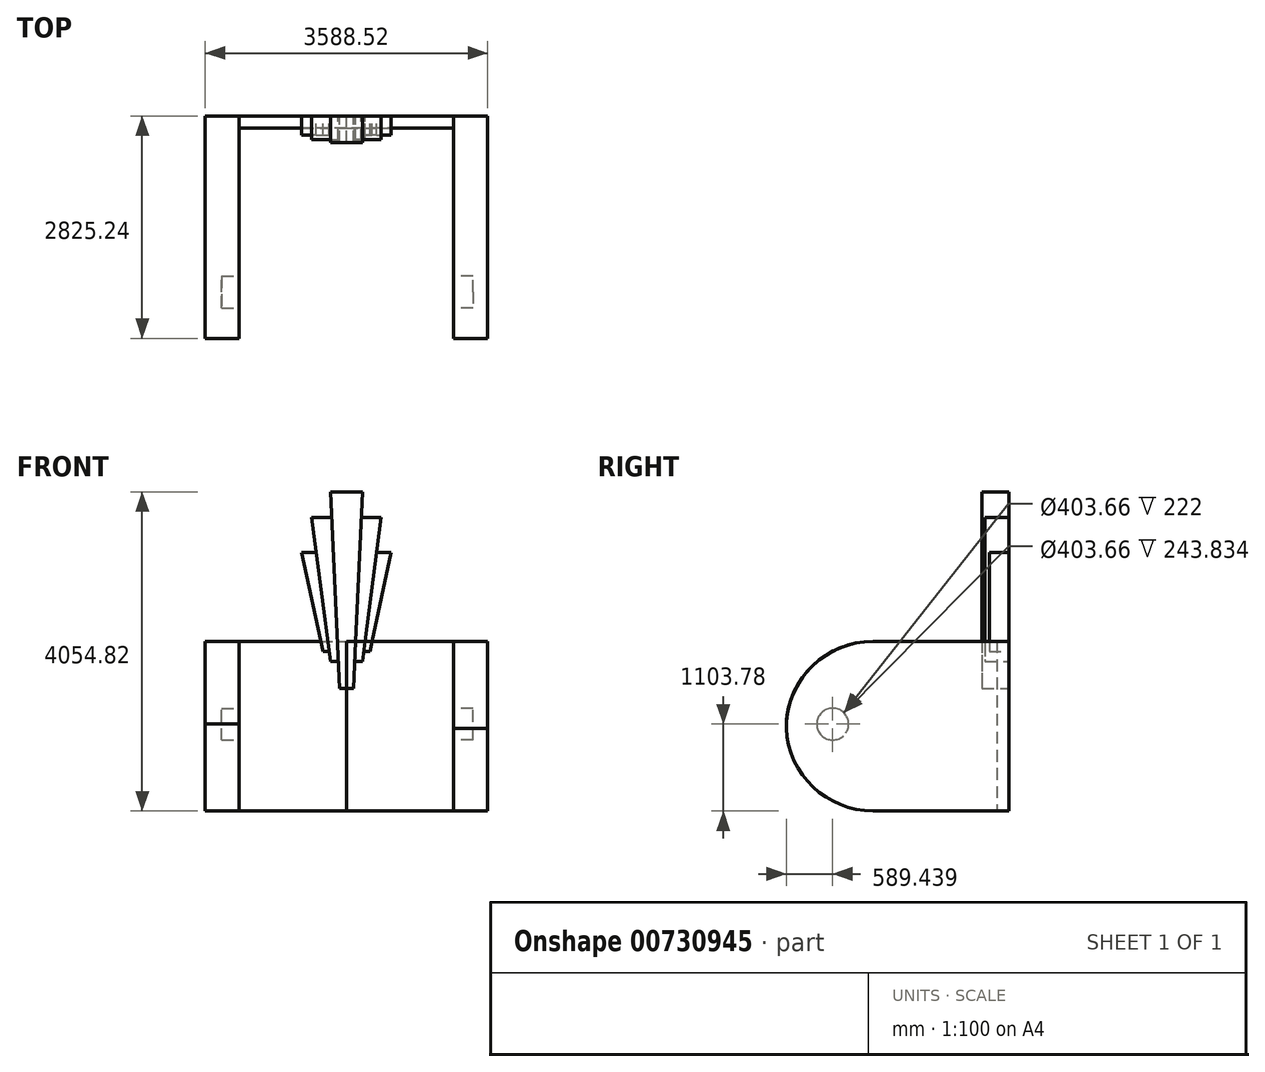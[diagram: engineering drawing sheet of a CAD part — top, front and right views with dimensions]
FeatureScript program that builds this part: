
annotation { "Feature Type Name" : "Feature", "Feature Type Description" : "" }
export const myFeature = defineFeature(function(context is Context, id is Id, definition is map)
    precondition{}
    {
        {
            var Q0;
            Q0=qCreatedBy(makeId("Front.planeOp"),FACE);
            var sketch = newSketch(context, id + "F0", { "sketchPlane" : qUnion([Q0])});
            skLineSegment(sketch, "E0", {"start": v(-1794.26, 1172.74) * mm, "end": v(1362.58, 1172.74) * mm});
            skLineSegment(sketch, "E1", {"start": v(1362.58, -982.7) * mm, "end": v(1362.58, 1172.74) * mm});
            skLineSegment(sketch, "E2", {"start": v(1362.58, -982.7) * mm, "end": v(-1794.26, -982.7) * mm});
            skLineSegment(sketch, "E3", {"start": v(-1794.26, 1172.74) * mm, "end": v(-1794.26, -982.7) * mm});
            skLineSegment(sketch, "E4", {"start": v(0, 1172.74) * mm, "end": v(0, -982.7) * mm});
            skLineSegment(sketch, "E5.MirrorCS", {"start": v(1794.26, 1172.74) * mm, "end": v(1794.26, -982.7) * mm});
            skLineSegment(sketch, "E6.MirrorCS", {"start": v(-1362.58, -982.7) * mm, "end": v(-1362.58, 1172.74) * mm});
            skLineSegment(sketch, "E7", {"start": v(1362.58, 1172.74) * mm, "end": v(1794.26, 1172.74) * mm});
            skLineSegment(sketch, "E8", {"start": v(1362.58, -982.7) * mm, "end": v(1794.26, -982.7) * mm});
            skSolve(sketch);
        }
        {
            var Q0;
            {var subQ0=sQuery(id+"F0.wireOp",EDGE,"E3");Q0=makeQuery(id+"F0.imprint","IMPRINT",FACE,{"disambiguationData":[TD([[makeQuery(id+"F0.imprint","IMPRINT",EDGE,{"derivedFrom":subQ0}),1.0]])]});}
            extrude(context, id + "F1", {"entities" : qUnion([Q0]), "depth" : 2825.24 * mm, "offsetDistance" : 25.4 * mm});
        }
        {
            var Q0;
            {var subQ0=sQuery(id+"F0.wireOp",EDGE,"E1");Q0=makeQuery(id+"F0.imprint","IMPRINT",FACE,{"disambiguationData":[TD([[makeQuery(id+"F0.imprint","IMPRINT",EDGE,{"derivedFrom":subQ0}),1.0]])]});}
            extrude(context, id + "F2", {"entities" : qUnion([Q0]), "depth" : 152.4 * mm, "offsetDistance" : 25.4 * mm});
        }
        {
            var Q0;
            Q0=makeQuery(id+"F1.opExtrude","CAP_EDGE",EDGE,{"disambiguationData":[OSD([sQuery(id+"F0.wireOp",EDGE,"E2")])],"isStart":false});
            fillet(context, id + "F3", {"entities" : qUnion([Q0]), "radius" : 1103.78 * mm, "tangentPropagation" : true, "allowEdgeOverflow" : false});
        }
        {
            var Q0;
            Q0=makeQuery(id+"F1.opExtrude","CAP_EDGE",EDGE,{"disambiguationData":[OSD([sQuery(id+"F0.wireOp",EDGE,"E0")])],"isStart":false});
            fillet(context, id + "F4", {"entities" : qUnion([Q0]), "radius" : 1103.78 * mm, "tangentPropagation" : true, "allowEdgeOverflow" : false});
        }
        {
            var Q0;
            Q0=makeQuery(id+"F2.opExtrude","CAP_FACE",FACE,{"disambiguationData":[OSD([sQuery(id+"F0.wireOp",EDGE,"E0"),sQuery(id+"F0.wireOp",EDGE,"E1"),sQuery(id+"F0.wireOp",EDGE,"E2"),sQuery(id+"F0.wireOp",EDGE,"sX38Ko4N-RZgO-N5hY-b6du-1SKDG1pY7xjY")])],"isStart":true});
            var sketch = newSketch(context, id + "F5", { "sketchPlane" : qUnion([Q0])});
            skLineSegment(sketch, "E9", {"start": v(0, 3072.12) * mm, "end": v(-202.15, 3072.12) * mm});
            skLineSegment(sketch, "E10", {"start": v(-202.15, 3072.12) * mm, "end": v(-89.06, 571.59) * mm});
            skLineSegment(sketch, "E11", {"start": v(-89.06, 571.59) * mm, "end": v(0, 571.59) * mm});
            skLineSegment(sketch, "E12.MirrorCS", {"start": v(202.15, 3072.12) * mm, "end": v(89.06, 571.59) * mm});
            skLineSegment(sketch, "E13.MirrorCS", {"start": v(0, 3072.12) * mm, "end": v(202.15, 3072.12) * mm});
            skLineSegment(sketch, "E14.MirrorCS", {"start": v(89.06, 571.59) * mm, "end": v(0, 571.59) * mm});
            skLineSegment(sketch, "E15", {"start": v(-187.3, 2743.87) * mm, "end": v(-442.01, 2743.87) * mm});
            skLineSegment(sketch, "E16", {"start": v(-442.01, 2743.87) * mm, "end": v(-202.15, 918.12) * mm});
            skLineSegment(sketch, "E17", {"start": v(-202.15, 918.12) * mm, "end": v(-104.73, 918.12) * mm});
            skLineSegment(sketch, "E18", {"start": v(-384.26, 2304.3) * mm, "end": v(-568.58, 2304.3) * mm});
            skLineSegment(sketch, "E19", {"start": v(-568.58, 2304.3) * mm, "end": v(-296.4, 1047.23) * mm});
            skLineSegment(sketch, "E20", {"start": v(-296.4, 1047.23) * mm, "end": v(-219.11, 1047.23) * mm});
            skLineSegment(sketch, "E21.MirrorCS", {"start": v(187.3, 2743.87) * mm, "end": v(442.01, 2743.87) * mm});
            skLineSegment(sketch, "E22.MirrorCS", {"start": v(442.01, 2743.87) * mm, "end": v(202.15, 918.12) * mm});
            skLineSegment(sketch, "E23.MirrorCS", {"start": v(384.26, 2304.3) * mm, "end": v(568.58, 2304.3) * mm});
            skLineSegment(sketch, "E24.MirrorCS", {"start": v(568.58, 2304.3) * mm, "end": v(296.4, 1047.23) * mm});
            skLineSegment(sketch, "E25.MirrorCS", {"start": v(296.4, 1047.23) * mm, "end": v(219.11, 1047.23) * mm});
            skLineSegment(sketch, "E26.MirrorCS", {"start": v(202.15, 918.12) * mm, "end": v(104.73, 918.12) * mm});
            skSolve(sketch);
        }
        {
            var Q0;
            {var subQ8=sQuery(id+"F5.wireOp",EDGE,"E9");Q0=makeQuery(id+"F5.imprint","IMPRINT",FACE,{"disambiguationData":[TD([[makeQuery(id+"F5.imprint","IMPRINT",EDGE,{"derivedFrom":subQ8}),1.0]])]});}
            extrude(context, id + "F6", {"entities" : qUnion([Q0]), "oppositeDirection" : true, "depth" : 337.82 * mm, "offsetDistance" : 25.4 * mm});
        }
        {
            var Q0;
            {var subQ0=sQuery(id+"F5.wireOp",EDGE,"E11");Q0=makeQuery(id+"F5.imprint","IMPRINT",FACE,{"disambiguationData":[TD([[makeQuery(id+"F5.imprint","IMPRINT",EDGE,{"derivedFrom":subQ0}),1.0]])]});}
            extrude(context, id + "F7", {"entities" : qUnion([Q0]), "oppositeDirection" : true, "depth" : 337.82 * mm, "offsetDistance" : 25.4 * mm});
        }
        {
            var Q0;
            {var subQ4=sQuery(id+"F5.wireOp",EDGE,"E15");Q0=makeQuery(id+"F5.imprint","IMPRINT",FACE,{"disambiguationData":[TD([[makeQuery(id+"F5.imprint","IMPRINT",EDGE,{"derivedFrom":subQ4}),1.0]])]});}
            extrude(context, id + "F8", {"entities" : qUnion([Q0]), "oppositeDirection" : true, "depth" : 299.72 * mm, "offsetDistance" : 25.4 * mm});
        }
        {
            var Q0;
            {var subQ0=sQuery(id+"F5.wireOp",EDGE,"E17");Q0=makeQuery(id+"F5.imprint","IMPRINT",FACE,{"disambiguationData":[TD([[makeQuery(id+"F5.imprint","IMPRINT",EDGE,{"derivedFrom":subQ0}),1.0]])]});}
            extrude(context, id + "F9", {"entities" : qUnion([Q0]), "oppositeDirection" : true, "depth" : 299.72 * mm, "offsetDistance" : 25.4 * mm});
        }
        {
            var Q0;
            {var subQ4=sQuery(id+"F5.wireOp",EDGE,"E21.MirrorCS");Q0=makeQuery(id+"F5.imprint","IMPRINT",FACE,{"disambiguationData":[TD([[makeQuery(id+"F5.imprint","IMPRINT",EDGE,{"derivedFrom":subQ4}),-1.0]])]});}
            extrude(context, id + "F10", {"entities" : qUnion([Q0]), "oppositeDirection" : true, "depth" : 299.72 * mm, "offsetDistance" : 25.4 * mm});
        }
        {
            var Q0;
            {var subQ0=sQuery(id+"F5.wireOp",EDGE,"E26.MirrorCS");Q0=makeQuery(id+"F5.imprint","IMPRINT",FACE,{"disambiguationData":[TD([[makeQuery(id+"F5.imprint","IMPRINT",EDGE,{"derivedFrom":subQ0}),-1.0]])]});}
            extrude(context, id + "F11", {"entities" : qUnion([Q0]), "oppositeDirection" : true, "depth" : 299.72 * mm, "offsetDistance" : 25.4 * mm});
        }
        {
            var Q0;
            {var subQ0=sQuery(id+"F5.wireOp",EDGE,"E18");Q0=makeQuery(id+"F5.imprint","IMPRINT",FACE,{"disambiguationData":[TD([[makeQuery(id+"F5.imprint","IMPRINT",EDGE,{"derivedFrom":subQ0}),1.0]])]});}
            extrude(context, id + "F12", {"entities" : qUnion([Q0]), "oppositeDirection" : true, "depth" : 246.38 * mm, "offsetDistance" : 25.4 * mm});
        }
        {
            var Q0;
            {var subQ0=sQuery(id+"F5.wireOp",EDGE,"E20");Q0=makeQuery(id+"F5.imprint","IMPRINT",FACE,{"disambiguationData":[TD([[makeQuery(id+"F5.imprint","IMPRINT",EDGE,{"derivedFrom":subQ0}),1.0]])]});}
            extrude(context, id + "F13", {"entities" : qUnion([Q0]), "oppositeDirection" : true, "depth" : 246.38 * mm, "offsetDistance" : 25.4 * mm});
        }
        {
            var Q0;
            {var subQ0=sQuery(id+"F5.wireOp",EDGE,"E23.MirrorCS");Q0=makeQuery(id+"F5.imprint","IMPRINT",FACE,{"disambiguationData":[TD([[makeQuery(id+"F5.imprint","IMPRINT",EDGE,{"derivedFrom":subQ0}),-1.0]])]});}
            extrude(context, id + "F14", {"entities" : qUnion([Q0]), "oppositeDirection" : true, "depth" : 246.38 * mm, "offsetDistance" : 25.4 * mm});
        }
        {
            var Q0;
            {var subQ0=sQuery(id+"F5.wireOp",EDGE,"E25.MirrorCS");Q0=makeQuery(id+"F5.imprint","IMPRINT",FACE,{"disambiguationData":[TD([[makeQuery(id+"F5.imprint","IMPRINT",EDGE,{"derivedFrom":subQ0}),-1.0]])]});}
            extrude(context, id + "F15", {"entities" : qUnion([Q0]), "oppositeDirection" : true, "depth" : 246.38 * mm, "offsetDistance" : 25.4 * mm});
        }
        {
            var Q0;
            {var subQ0=sQuery(id+"F0.wireOp",EDGE,"E4");Q0=makeQuery(id+"F0.imprint","IMPRINT",FACE,{"disambiguationData":[TD([[makeQuery(id+"F0.imprint","IMPRINT",EDGE,{"derivedFrom":subQ0}),-1.0]])]});}
            extrude(context, id + "F16", {"entities" : qUnion([Q0]), "depth" : 152.4 * mm, "offsetDistance" : 25.4 * mm});
        }
        {
            var Q0;
            Q0=makeQuery(id+"F0.imprint","IMPRINT",FACE,{"disambiguationData":[TD([[makeQuery(id+"F0.imprint","IMPRINT",EDGE,{"derivedFrom":sQuery(id+"F0.wireOp",EDGE,"E1")}),-1.0]])]});
            extrude(context, id + "F17", {"entities" : qUnion([Q0]), "depth" : 2825.24 * mm, "offsetDistance" : 25.4 * mm});
        }
        {
            var Q0;
            Q0=makeQuery(id+"F17.opExtrude","CAP_EDGE",EDGE,{"disambiguationData":[OSD([sQuery(id+"F0.wireOp",EDGE,"E7")])],"isStart":false});
            fillet(context, id + "F18", {"entities" : qUnion([Q0]), "radius" : 1103.78 * mm, "tangentPropagation" : true, "allowEdgeOverflow" : false});
        }
        {
            var Q0;
            Q0=makeQuery(id+"F17.opExtrude","CAP_EDGE",EDGE,{"disambiguationData":[OSD([sQuery(id+"F0.wireOp",EDGE,"E8")])],"isStart":false});
            fillet(context, id + "F19", {"entities" : qUnion([Q0]), "radius" : 1103.78 * mm, "tangentPropagation" : true, "allowEdgeOverflow" : false});
        }
        {
            var Q0;
            Q0=makeQuery(id+"F1.opExtrude","SWEPT_FACE",FACE,{"disambiguationData":[OSD([sQuery(id+"F0.wireOp",EDGE,"E6.MirrorCS")])]});
            var sketch = newSketch(context, id + "F20", { "sketchPlane" : qUnion([Q0])});
            skCircle(sketch, "E27", {"center": v(-2235.8, 121.08) * mm, "radius": 201.83 * mm});
            skSolve(sketch);
        }
        {
            var Q0;
            Q0=makeQuery(id+"F20.imprint","IMPRINT",FACE,{"disambiguationData":[TD([[makeQuery(id+"F20.imprint","IMPRINT",EDGE,{"derivedFrom":sQuery(id+"F20.wireOp",EDGE,"E27")}),1.0]])]});
            extrude(context, id + "F21", {"entities" : qUnion([Q0]), "operationType" : NewBodyOperationType.REMOVE, "oppositeDirection" : true, "depth" : 222 * mm, "offsetDistance" : 25 * mm});
        }
        {
            var Q0;
            Q0=makeQuery(id+"F20.imprint","IMPRINT",FACE,{"disambiguationData":[TD([[makeQuery(id+"F20.imprint","IMPRINT",EDGE,{"derivedFrom":sQuery(id+"F20.wireOp",EDGE,"E27")}),1.0]])]});
            extrude(context, id + "F22", {"entities" : qUnion([Q0]), "operationType" : NewBodyOperationType.REMOVE, "depth" : 2969 * mm, "offsetDistance" : 25 * mm});
        }
    });
